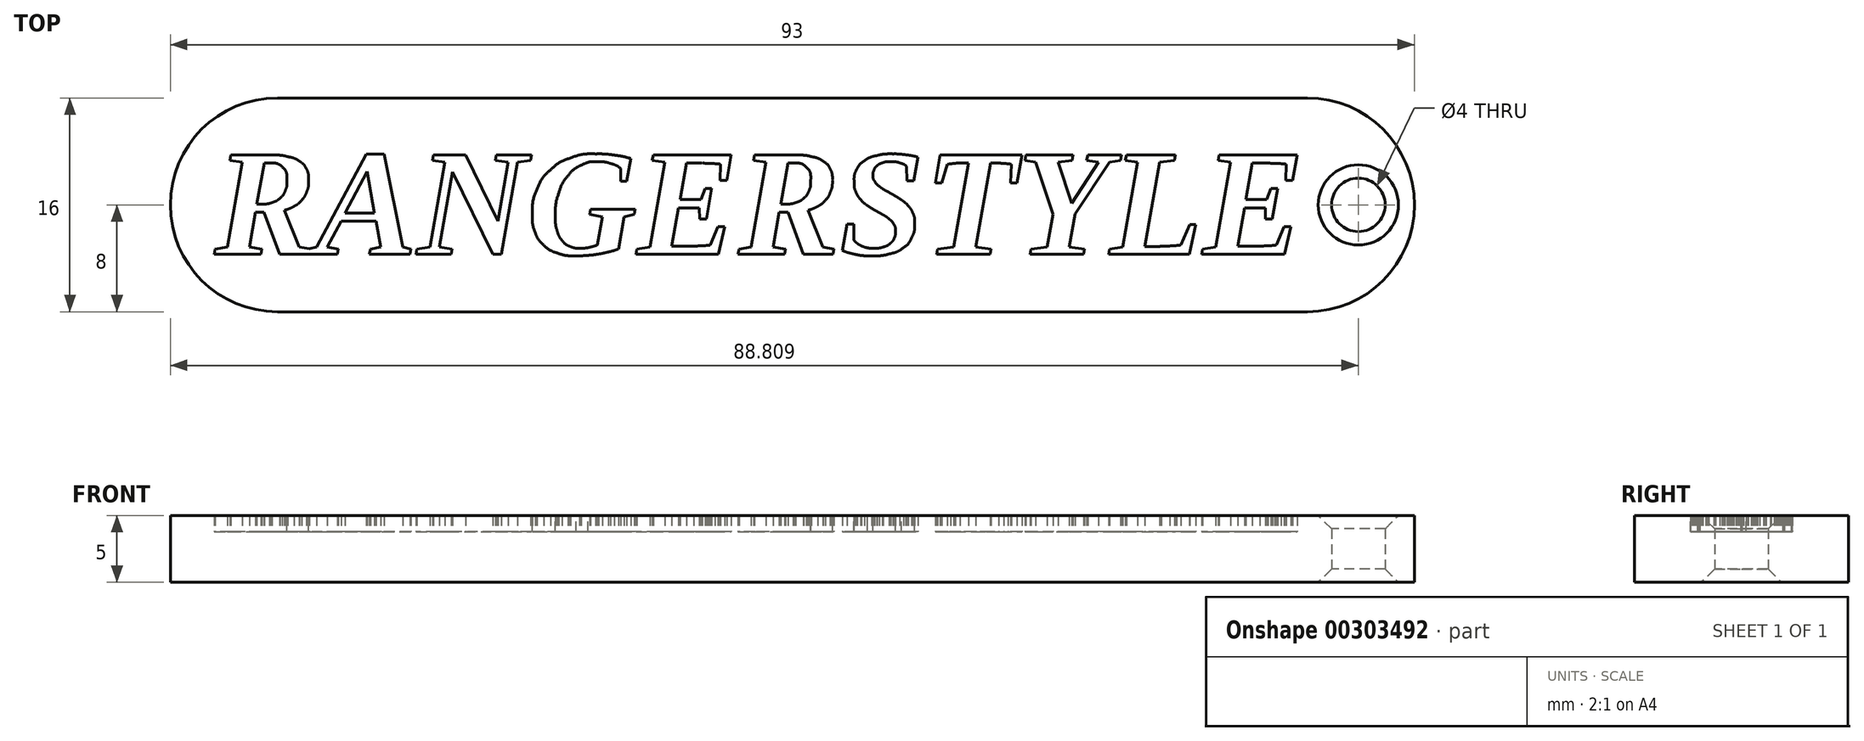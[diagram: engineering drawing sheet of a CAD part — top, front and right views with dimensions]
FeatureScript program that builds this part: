
annotation { "Feature Type Name" : "Feature", "Feature Type Description" : "" }
export const myFeature = defineFeature(function(context is Context, id is Id, definition is map)
    precondition{}
    {
        {
            var Q0;
            Q0=qCreatedBy(makeId("Top.planeOp"),FACE);
            var sketch = newSketch(context, id + "F0", { "sketchPlane" : qUnion([Q0])});
            skFitSpline(sketch, "E0", {"points": [v(-36.27, 3.73) * mm, v(-35.77, 3.73) * mm, v(-35.34, 3.69) * mm, v(-34.99, 3.6) * mm]});
            skFitSpline(sketch, "E1", {"points": [v(-34.99, 3.6) * mm, v(-34.63, 3.53) * mm, v(-34.33, 3.41) * mm, v(-34.1, 3.25) * mm]});
            skFitSpline(sketch, "E2", {"points": [v(-34.1, 3.25) * mm, v(-33.87, 3.1) * mm, v(-33.7, 2.9) * mm, v(-33.59, 2.67) * mm]});
            skFitSpline(sketch, "E3", {"points": [v(-33.59, 2.67) * mm, v(-33.48, 2.44) * mm, v(-33.42, 2.17) * mm, v(-33.42, 1.86) * mm]});
            skFitSpline(sketch, "E4", {"points": [v(-33.42, 1.86) * mm, v(-33.42, 1.54) * mm, v(-33.47, 1.25) * mm, v(-33.56, 1) * mm]});
            skFitSpline(sketch, "E5", {"points": [v(-33.56, 1) * mm, v(-33.65, 0.75) * mm, v(-33.78, 0.53) * mm, v(-33.94, 0.35) * mm]});
            skFitSpline(sketch, "E6", {"points": [v(-33.94, 0.35) * mm, v(-34.1, 0.17) * mm, v(-34.3, 0.01) * mm, v(-34.53, -0.11) * mm]});
            skFitSpline(sketch, "E7", {"points": [v(-34.53, -0.11) * mm, v(-34.75, -0.23) * mm, v(-34.99, -0.33) * mm, v(-35.25, -0.4) * mm]});
            skLineSegment(sketch, "E8", {"start": v(-37.4, -0.55) * mm, "end": v(-37.86, -3.15) * mm});
            skLineSegment(sketch, "E9", {"start": v(-37.86, -3.15) * mm, "end": v(-36.93, -3.3) * mm});
            skLineSegment(sketch, "E10", {"start": v(-36.93, -3.3) * mm, "end": v(-37, -3.7) * mm});
            skLineSegment(sketch, "E11", {"start": v(-37, -3.7) * mm, "end": v(-40.47, -3.7) * mm});
            skLineSegment(sketch, "E12", {"start": v(-40.47, -3.7) * mm, "end": v(-40.4, -3.3) * mm});
            skLineSegment(sketch, "E13", {"start": v(-40.4, -3.3) * mm, "end": v(-39.5, -3.15) * mm});
            skLineSegment(sketch, "E14", {"start": v(-39.5, -3.15) * mm, "end": v(-38.38, 3.18) * mm});
            skLineSegment(sketch, "E15", {"start": v(-38.38, 3.18) * mm, "end": v(-39.3, 3.33) * mm});
            skLineSegment(sketch, "E16", {"start": v(-39.3, 3.33) * mm, "end": v(-39.24, 3.73) * mm});
            skLineSegment(sketch, "E17", {"start": v(-39.24, 3.73) * mm, "end": v(-36.27, 3.73) * mm});
            skFitSpline(sketch, "E18", {"points": [v(-36.99, 0.06) * mm, v(-36.68, 0.06) * mm, v(-36.41, 0.1) * mm, v(-36.17, 0.17) * mm]});
            skFitSpline(sketch, "E19", {"points": [v(-36.17, 0.17) * mm, v(-35.93, 0.25) * mm, v(-35.73, 0.36) * mm, v(-35.56, 0.5) * mm]});
            skFitSpline(sketch, "E20", {"points": [v(-35.56, 0.5) * mm, v(-35.4, 0.65) * mm, v(-35.27, 0.83) * mm, v(-35.18, 1.04) * mm]});
            skFitSpline(sketch, "E21", {"points": [v(-35.18, 1.04) * mm, v(-35.1, 1.26) * mm, v(-35.05, 1.5) * mm, v(-35.05, 1.77) * mm]});
            skFitSpline(sketch, "E22", {"points": [v(-35.05, 1.77) * mm, v(-35.05, 2.25) * mm, v(-35.16, 2.6) * mm, v(-35.39, 2.8) * mm]});
            skFitSpline(sketch, "E23", {"points": [v(-35.39, 2.8) * mm, v(-35.6, 3.02) * mm, v(-35.93, 3.12) * mm, v(-36.37, 3.12) * mm]});
            skLineSegment(sketch, "E24", {"start": v(-35.25, -0.4) * mm, "end": v(-34.13, -3.15) * mm});
            skLineSegment(sketch, "E25", {"start": v(-34.13, -3.15) * mm, "end": v(-33.32, -3.3) * mm});
            skLineSegment(sketch, "E26", {"start": v(-33.32, -3.3) * mm, "end": v(-33.38, -3.7) * mm});
            skLineSegment(sketch, "E27", {"start": v(-33.38, -3.7) * mm, "end": v(-35.6, -3.7) * mm});
            skLineSegment(sketch, "E28", {"start": v(-35.6, -3.7) * mm, "end": v(-36.75, -0.55) * mm});
            skLineSegment(sketch, "E29", {"start": v(-36.75, -0.55) * mm, "end": v(-37.4, -0.55) * mm});
            skLineSegment(sketch, "E30", {"start": v(-36.37, 3.12) * mm, "end": v(-36.75, 3.12) * mm});
            skLineSegment(sketch, "E31", {"start": v(-36.75, 3.12) * mm, "end": v(-37.3, 0.06) * mm});
            skLineSegment(sketch, "E32", {"start": v(-37.3, 0.06) * mm, "end": v(-36.99, 0.06) * mm});
            skLineSegment(sketch, "E33", {"start": v(-31.2, -3.3) * mm, "end": v(-31.28, -3.7) * mm});
            skLineSegment(sketch, "E34", {"start": v(-31.28, -3.7) * mm, "end": v(-33.46, -3.7) * mm});
            skLineSegment(sketch, "E35", {"start": v(-33.46, -3.7) * mm, "end": v(-33.38, -3.3) * mm});
            skLineSegment(sketch, "E36", {"start": v(-33.38, -3.3) * mm, "end": v(-32.81, -3.15) * mm});
            skLineSegment(sketch, "E37", {"start": v(-32.81, -3.15) * mm, "end": v(-29.11, 3.8) * mm});
            skLineSegment(sketch, "E38", {"start": v(-29.11, 3.8) * mm, "end": v(-27.78, 3.8) * mm});
            skLineSegment(sketch, "E39", {"start": v(-27.78, 3.8) * mm, "end": v(-26.37, -3.15) * mm});
            skLineSegment(sketch, "E40", {"start": v(-26.37, -3.15) * mm, "end": v(-25.77, -3.3) * mm});
            skLineSegment(sketch, "E41", {"start": v(-25.77, -3.3) * mm, "end": v(-25.85, -3.7) * mm});
            skLineSegment(sketch, "E42", {"start": v(-25.85, -3.7) * mm, "end": v(-28.89, -3.7) * mm});
            skLineSegment(sketch, "E43", {"start": v(-28.89, -3.7) * mm, "end": v(-28.81, -3.3) * mm});
            skLineSegment(sketch, "E44", {"start": v(-28.81, -3.3) * mm, "end": v(-28.05, -3.15) * mm});
            skLineSegment(sketch, "E45", {"start": v(-28.05, -3.15) * mm, "end": v(-28.38, -1.22) * mm});
            skLineSegment(sketch, "E46", {"start": v(-28.38, -1.22) * mm, "end": v(-31, -1.22) * mm});
            skLineSegment(sketch, "E47", {"start": v(-31, -1.22) * mm, "end": v(-32.02, -3.15) * mm});
            skLineSegment(sketch, "E48", {"start": v(-32.02, -3.15) * mm, "end": v(-31.2, -3.3) * mm});
            skLineSegment(sketch, "E49", {"start": v(-29.06, 2.5) * mm, "end": v(-30.7, -0.62) * mm});
            skLineSegment(sketch, "E50", {"start": v(-30.7, -0.62) * mm, "end": v(-28.5, -0.62) * mm});
            skLineSegment(sketch, "E51", {"start": v(-28.5, -0.62) * mm, "end": v(-29.06, 2.5) * mm});
            skFitSpline(sketch, "E52", {"points": [v(-16.7, -0.8) * mm, v(-16.7, -0.06) * mm, v(-16.58, 0.6) * mm, v(-16.34, 1.17) * mm]});
            skFitSpline(sketch, "E53", {"points": [v(-16.34, 1.17) * mm, v(-16.1, 1.74) * mm, v(-15.76, 2.22) * mm, v(-15.34, 2.62) * mm]});
            skFitSpline(sketch, "E54", {"points": [v(-15.34, 2.62) * mm, v(-14.91, 3) * mm, v(-14.41, 3.3) * mm, v(-13.83, 3.5) * mm]});
            skFitSpline(sketch, "E55", {"points": [v(-13.83, 3.5) * mm, v(-13.26, 3.71) * mm, v(-12.64, 3.81) * mm, v(-11.97, 3.81) * mm]});
            skFitSpline(sketch, "E56", {"points": [v(-11.97, 3.81) * mm, v(-11.46, 3.81) * mm, v(-10.99, 3.78) * mm, v(-10.56, 3.72) * mm]});
            skFitSpline(sketch, "E57", {"points": [v(-10.56, 3.72) * mm, v(-10.14, 3.66) * mm, v(-9.73, 3.58) * mm, v(-9.33, 3.47) * mm]});
            skLineSegment(sketch, "E58", {"start": v(-18.5, 3.18) * mm, "end": v(-19.47, 3.33) * mm});
            skLineSegment(sketch, "E59", {"start": v(-19.47, 3.33) * mm, "end": v(-19.4, 3.73) * mm});
            skLineSegment(sketch, "E60", {"start": v(-19.4, 3.73) * mm, "end": v(-16.76, 3.73) * mm});
            skLineSegment(sketch, "E61", {"start": v(-16.76, 3.73) * mm, "end": v(-16.83, 3.33) * mm});
            skLineSegment(sketch, "E62", {"start": v(-16.83, 3.33) * mm, "end": v(-17.8, 3.18) * mm});
            skLineSegment(sketch, "E63", {"start": v(-17.8, 3.18) * mm, "end": v(-19.02, -3.7) * mm});
            skLineSegment(sketch, "E64", {"start": v(-19.02, -3.7) * mm, "end": v(-19.65, -3.7) * mm});
            skLineSegment(sketch, "E65", {"start": v(-19.65, -3.7) * mm, "end": v(-22.65, 2.46) * mm});
            skLineSegment(sketch, "E66", {"start": v(-22.65, 2.46) * mm, "end": v(-23.66, -3.15) * mm});
            skLineSegment(sketch, "E67", {"start": v(-23.66, -3.15) * mm, "end": v(-22.69, -3.3) * mm});
            skLineSegment(sketch, "E68", {"start": v(-22.69, -3.3) * mm, "end": v(-22.75, -3.7) * mm});
            skLineSegment(sketch, "E69", {"start": v(-22.75, -3.7) * mm, "end": v(-25.4, -3.7) * mm});
            skLineSegment(sketch, "E70", {"start": v(-25.4, -3.7) * mm, "end": v(-25.33, -3.3) * mm});
            skLineSegment(sketch, "E71", {"start": v(-25.33, -3.3) * mm, "end": v(-24.35, -3.15) * mm});
            skLineSegment(sketch, "E72", {"start": v(-24.35, -3.15) * mm, "end": v(-23.24, 3.18) * mm});
            skLineSegment(sketch, "E73", {"start": v(-23.24, 3.18) * mm, "end": v(-24.16, 3.33) * mm});
            skLineSegment(sketch, "E74", {"start": v(-24.16, 3.33) * mm, "end": v(-24.09, 3.73) * mm});
            skLineSegment(sketch, "E75", {"start": v(-24.09, 3.73) * mm, "end": v(-21.69, 3.73) * mm});
            skLineSegment(sketch, "E76", {"start": v(-21.69, 3.73) * mm, "end": v(-19.28, -1.22) * mm});
            skLineSegment(sketch, "E77", {"start": v(-19.28, -1.22) * mm, "end": v(-18.5, 3.18) * mm});
            skFitSpline(sketch, "E78", {"points": [v(-10.1, 2.73) * mm, v(-10.31, 2.89) * mm, v(-10.57, 3.01) * mm, v(-10.87, 3.1) * mm]});
            skFitSpline(sketch, "E79", {"points": [v(-10.87, 3.1) * mm, v(-11.17, 3.19) * mm, v(-11.5, 3.23) * mm, v(-11.87, 3.23) * mm]});
            skFitSpline(sketch, "E80", {"points": [v(-11.87, 3.23) * mm, v(-12.29, 3.23) * mm, v(-12.68, 3.14) * mm, v(-13.06, 2.96) * mm]});
            skFitSpline(sketch, "E81", {"points": [v(-13.06, 2.96) * mm, v(-13.43, 2.78) * mm, v(-13.76, 2.51) * mm, v(-14.05, 2.16) * mm]});
            skFitSpline(sketch, "E82", {"points": [v(-14.05, 2.16) * mm, v(-14.33, 1.81) * mm, v(-14.56, 1.38) * mm, v(-14.73, 0.86) * mm]});
            skFitSpline(sketch, "E83", {"points": [v(-14.73, 0.86) * mm, v(-14.9, 0.35) * mm, v(-14.98, -0.25) * mm, v(-14.98, -0.91) * mm]});
            skFitSpline(sketch, "E84", {"points": [v(-14.98, -0.91) * mm, v(-14.98, -1.3) * mm, v(-14.93, -1.64) * mm, v(-14.84, -1.93) * mm]});
            skFitSpline(sketch, "E85", {"points": [v(-14.84, -1.93) * mm, v(-14.76, -2.23) * mm, v(-14.63, -2.47) * mm, v(-14.47, -2.67) * mm]});
            skFitSpline(sketch, "E86", {"points": [v(-14.47, -2.67) * mm, v(-14.31, -2.86) * mm, v(-14.12, -3) * mm, v(-13.9, -3.1) * mm]});
            skFitSpline(sketch, "E87", {"points": [v(-13.9, -3.1) * mm, v(-13.68, -3.2) * mm, v(-13.43, -3.24) * mm, v(-13.16, -3.24) * mm]});
            skFitSpline(sketch, "E88", {"points": [v(-13.16, -3.24) * mm, v(-12.88, -3.24) * mm, v(-12.62, -3.22) * mm, v(-12.4, -3.16) * mm]});
            skFitSpline(sketch, "E89", {"points": [v(-12.4, -3.16) * mm, v(-12.16, -3.1) * mm, v(-11.98, -3.06) * mm, v(-11.85, -3) * mm]});
            skLineSegment(sketch, "E90", {"start": v(-9.33, 3.47) * mm, "end": v(-9.64, 1.76) * mm});
            skLineSegment(sketch, "E91", {"start": v(-9.64, 1.76) * mm, "end": v(-10.1, 1.76) * mm});
            skLineSegment(sketch, "E92", {"start": v(-10.1, 1.76) * mm, "end": v(-10.1, 2.73) * mm});
            skFitSpline(sketch, "E93", {"points": [v(-10.27, -3.31) * mm, v(-10.51, -3.4) * mm, v(-10.76, -3.46) * mm, v(-11, -3.53) * mm]});
            skFitSpline(sketch, "E94", {"points": [v(-11, -3.53) * mm, v(-11.25, -3.58) * mm, v(-11.5, -3.64) * mm, v(-11.76, -3.68) * mm]});
            skFitSpline(sketch, "E95", {"points": [v(-11.76, -3.68) * mm, v(-12.01, -3.72) * mm, v(-12.28, -3.76) * mm, v(-12.55, -3.78) * mm]});
            skFitSpline(sketch, "E96", {"points": [v(-12.55, -3.78) * mm, v(-12.83, -3.8) * mm, v(-13.12, -3.81) * mm, v(-13.42, -3.81) * mm]});
            skFitSpline(sketch, "E97", {"points": [v(-13.42, -3.81) * mm, v(-13.94, -3.81) * mm, v(-14.41, -3.75) * mm, v(-14.82, -3.6) * mm]});
            skFitSpline(sketch, "E98", {"points": [v(-14.82, -3.6) * mm, v(-15.23, -3.47) * mm, v(-15.57, -3.27) * mm, v(-15.85, -3) * mm]});
            skFitSpline(sketch, "E99", {"points": [v(-15.85, -3) * mm, v(-16.13, -2.75) * mm, v(-16.34, -2.43) * mm, v(-16.48, -2.06) * mm]});
            skFitSpline(sketch, "E100", {"points": [v(-16.48, -2.06) * mm, v(-16.63, -1.69) * mm, v(-16.7, -1.27) * mm, v(-16.7, -0.8) * mm]});
            skLineSegment(sketch, "E101", {"start": v(-11.85, -3) * mm, "end": v(-11.47, -0.9) * mm});
            skLineSegment(sketch, "E102", {"start": v(-11.47, -0.9) * mm, "end": v(-12.4, -0.72) * mm});
            skLineSegment(sketch, "E103", {"start": v(-12.4, -0.72) * mm, "end": v(-12.33, -0.34) * mm});
            skLineSegment(sketch, "E104", {"start": v(-12.33, -0.34) * mm, "end": v(-9.02, -0.34) * mm});
            skLineSegment(sketch, "E105", {"start": v(-9.02, -0.34) * mm, "end": v(-9.08, -0.72) * mm});
            skLineSegment(sketch, "E106", {"start": v(-9.08, -0.72) * mm, "end": v(-9.84, -0.9) * mm});
            skLineSegment(sketch, "E107", {"start": v(-9.84, -0.9) * mm, "end": v(-10.27, -3.31) * mm});
            skFitSpline(sketch, "E108", {"points": [v(-2.63, 3.04) * mm, v(-2.75, 3.06) * mm, v(-2.88, 3.07) * mm, v(-3.04, 3.08) * mm]});
            skFitSpline(sketch, "E109", {"points": [v(-3.04, 3.08) * mm, v(-3.19, 3.1) * mm, v(-3.35, 3.1) * mm, v(-3.51, 3.1) * mm]});
            skFitSpline(sketch, "E110", {"points": [v(-3.51, 3.1) * mm, v(-3.68, 3.11) * mm, v(-3.84, 3.12) * mm, v(-4, 3.12) * mm]});
            skFitSpline(sketch, "E111", {"points": [v(-4, 3.12) * mm, v(-4.15, 3.12) * mm, v(-4.3, 3.12) * mm, v(-4.41, 3.12) * mm]});
            skLineSegment(sketch, "E112", {"start": v(-8.9, -3.3) * mm, "end": v(-7.92, -3.15) * mm});
            skLineSegment(sketch, "E113", {"start": v(-7.92, -3.15) * mm, "end": v(-6.8, 3.18) * mm});
            skLineSegment(sketch, "E114", {"start": v(-6.8, 3.18) * mm, "end": v(-7.73, 3.33) * mm});
            skLineSegment(sketch, "E115", {"start": v(-7.73, 3.33) * mm, "end": v(-7.66, 3.73) * mm});
            skLineSegment(sketch, "E116", {"start": v(-7.66, 3.73) * mm, "end": v(-1.83, 3.73) * mm});
            skLineSegment(sketch, "E117", {"start": v(-1.83, 3.73) * mm, "end": v(-2.16, 1.84) * mm});
            skLineSegment(sketch, "E118", {"start": v(-2.16, 1.84) * mm, "end": v(-2.67, 1.84) * mm});
            skLineSegment(sketch, "E119", {"start": v(-2.67, 1.84) * mm, "end": v(-2.63, 3.04) * mm});
            skFitSpline(sketch, "E120", {"points": [v(-5.26, -3.1) * mm, v(-5.03, -3.1) * mm, v(-4.82, -3.1) * mm, v(-4.62, -3.09) * mm]});
            skFitSpline(sketch, "E121", {"points": [v(-4.62, -3.09) * mm, v(-4.41, -3.08) * mm, v(-4.23, -3.07) * mm, v(-4.07, -3.07) * mm]});
            skFitSpline(sketch, "E122", {"points": [v(-4.07, -3.07) * mm, v(-3.9, -3.06) * mm, v(-3.77, -3.05) * mm, v(-3.65, -3.04) * mm]});
            skFitSpline(sketch, "E123", {"points": [v(-3.65, -3.04) * mm, v(-3.53, -3.03) * mm, v(-3.45, -3.02) * mm, v(-3.39, -3) * mm]});
            skLineSegment(sketch, "E124", {"start": v(-4.41, 3.12) * mm, "end": v(-5.18, 3.12) * mm});
            skLineSegment(sketch, "E125", {"start": v(-5.18, 3.12) * mm, "end": v(-5.66, 0.4) * mm});
            skLineSegment(sketch, "E126", {"start": v(-5.66, 0.4) * mm, "end": v(-4.1, 0.4) * mm});
            skLineSegment(sketch, "E127", {"start": v(-4.1, 0.4) * mm, "end": v(-3.79, 1.21) * mm});
            skLineSegment(sketch, "E128", {"start": v(-3.79, 1.21) * mm, "end": v(-3.3, 1.21) * mm});
            skLineSegment(sketch, "E129", {"start": v(-3.3, 1.21) * mm, "end": v(-3.7, -1.07) * mm});
            skLineSegment(sketch, "E130", {"start": v(-3.7, -1.07) * mm, "end": v(-4.2, -1.07) * mm});
            skLineSegment(sketch, "E131", {"start": v(-4.2, -1.07) * mm, "end": v(-4.21, -0.23) * mm});
            skLineSegment(sketch, "E132", {"start": v(-4.21, -0.23) * mm, "end": v(-5.77, -0.23) * mm});
            skLineSegment(sketch, "E133", {"start": v(-5.77, -0.23) * mm, "end": v(-6.27, -3.1) * mm});
            skLineSegment(sketch, "E134", {"start": v(-6.27, -3.1) * mm, "end": v(-5.26, -3.1) * mm});
            skLineSegment(sketch, "E135", {"start": v(-3.39, -3) * mm, "end": v(-2.82, -1.63) * mm});
            skLineSegment(sketch, "E136", {"start": v(-2.82, -1.63) * mm, "end": v(-2.31, -1.63) * mm});
            skLineSegment(sketch, "E137", {"start": v(-2.31, -1.63) * mm, "end": v(-2.78, -3.7) * mm});
            skLineSegment(sketch, "E138", {"start": v(-2.78, -3.7) * mm, "end": v(-8.97, -3.7) * mm});
            skLineSegment(sketch, "E139", {"start": v(-8.97, -3.7) * mm, "end": v(-8.9, -3.3) * mm});
            skLineSegment(sketch, "E140", {"start": v(-8.9, -3.3) * mm, "end": v(-8.9, -3.3) * mm});
            skLineSegment(sketch, "E141", {"start": v(-5.04, -3.1) * mm, "end": v(-3.39, -3) * mm});
            skFitSpline(sketch, "E142", {"points": [v(2.88, 3.73) * mm, v(3.38, 3.73) * mm, v(3.8, 3.69) * mm, v(4.17, 3.6) * mm]});
            skFitSpline(sketch, "E143", {"points": [v(4.17, 3.6) * mm, v(4.53, 3.53) * mm, v(4.82, 3.41) * mm, v(5.05, 3.25) * mm]});
            skFitSpline(sketch, "E144", {"points": [v(5.05, 3.25) * mm, v(5.28, 3.1) * mm, v(5.45, 2.9) * mm, v(5.57, 2.67) * mm]});
            skFitSpline(sketch, "E145", {"points": [v(5.57, 2.67) * mm, v(5.68, 2.44) * mm, v(5.73, 2.17) * mm, v(5.73, 1.86) * mm]});
            skFitSpline(sketch, "E146", {"points": [v(5.73, 1.86) * mm, v(5.73, 1.54) * mm, v(5.69, 1.25) * mm, v(5.6, 1) * mm]});
            skFitSpline(sketch, "E147", {"points": [v(5.6, 1) * mm, v(5.5, 0.75) * mm, v(5.37, 0.53) * mm, v(5.21, 0.35) * mm]});
            skFitSpline(sketch, "E148", {"points": [v(5.21, 0.35) * mm, v(5.05, 0.17) * mm, v(4.85, 0.01) * mm, v(4.63, -0.11) * mm]});
            skFitSpline(sketch, "E149", {"points": [v(4.63, -0.11) * mm, v(4.4, -0.23) * mm, v(4.17, -0.33) * mm, v(3.9, -0.4) * mm]});
            skLineSegment(sketch, "E150", {"start": v(1.76, -0.55) * mm, "end": v(1.3, -3.15) * mm});
            skLineSegment(sketch, "E151", {"start": v(1.3, -3.15) * mm, "end": v(2.22, -3.3) * mm});
            skLineSegment(sketch, "E152", {"start": v(2.22, -3.3) * mm, "end": v(2.16, -3.7) * mm});
            skLineSegment(sketch, "E153", {"start": v(2.16, -3.7) * mm, "end": v(-1.32, -3.7) * mm});
            skLineSegment(sketch, "E154", {"start": v(-1.32, -3.7) * mm, "end": v(-1.25, -3.3) * mm});
            skLineSegment(sketch, "E155", {"start": v(-1.25, -3.3) * mm, "end": v(-0.34, -3.15) * mm});
            skLineSegment(sketch, "E156", {"start": v(-0.34, -3.15) * mm, "end": v(0.77, 3.18) * mm});
            skLineSegment(sketch, "E157", {"start": v(0.77, 3.18) * mm, "end": v(-0.16, 3.33) * mm});
            skLineSegment(sketch, "E158", {"start": v(-0.16, 3.33) * mm, "end": v(-0.08, 3.73) * mm});
            skLineSegment(sketch, "E159", {"start": v(-0.08, 3.73) * mm, "end": v(2.88, 3.73) * mm});
            skFitSpline(sketch, "E160", {"points": [v(2.17, 0.06) * mm, v(2.47, 0.06) * mm, v(2.74, 0.1) * mm, v(2.98, 0.17) * mm]});
            skFitSpline(sketch, "E161", {"points": [v(2.98, 0.17) * mm, v(3.22, 0.25) * mm, v(3.43, 0.36) * mm, v(3.6, 0.5) * mm]});
            skFitSpline(sketch, "E162", {"points": [v(3.6, 0.5) * mm, v(3.76, 0.65) * mm, v(3.89, 0.83) * mm, v(3.97, 1.04) * mm]});
            skFitSpline(sketch, "E163", {"points": [v(3.97, 1.04) * mm, v(4.06, 1.26) * mm, v(4.1, 1.5) * mm, v(4.1, 1.77) * mm]});
            skFitSpline(sketch, "E164", {"points": [v(4.1, 1.77) * mm, v(4.1, 2.25) * mm, v(4, 2.6) * mm, v(3.77, 2.8) * mm]});
            skFitSpline(sketch, "E165", {"points": [v(3.77, 2.8) * mm, v(3.55, 3.02) * mm, v(3.22, 3.12) * mm, v(2.79, 3.12) * mm]});
            skLineSegment(sketch, "E166", {"start": v(3.9, -0.4) * mm, "end": v(5.02, -3.15) * mm});
            skLineSegment(sketch, "E167", {"start": v(5.02, -3.15) * mm, "end": v(5.84, -3.3) * mm});
            skLineSegment(sketch, "E168", {"start": v(5.84, -3.3) * mm, "end": v(5.77, -3.7) * mm});
            skLineSegment(sketch, "E169", {"start": v(5.77, -3.7) * mm, "end": v(3.55, -3.7) * mm});
            skLineSegment(sketch, "E170", {"start": v(3.55, -3.7) * mm, "end": v(2.4, -0.55) * mm});
            skLineSegment(sketch, "E171", {"start": v(2.4, -0.55) * mm, "end": v(1.76, -0.55) * mm});
            skFitSpline(sketch, "E172", {"points": [v(8.67, -3.81) * mm, v(8.2, -3.81) * mm, v(7.76, -3.77) * mm, v(7.4, -3.7) * mm]});
            skFitSpline(sketch, "E173", {"points": [v(7.4, -3.7) * mm, v(7.03, -3.6) * mm, v(6.73, -3.52) * mm, v(6.49, -3.42) * mm]});
            skLineSegment(sketch, "E174", {"start": v(2.79, 3.12) * mm, "end": v(2.4, 3.12) * mm});
            skLineSegment(sketch, "E175", {"start": v(2.4, 3.12) * mm, "end": v(1.86, 0.06) * mm});
            skLineSegment(sketch, "E176", {"start": v(1.86, 0.06) * mm, "end": v(2.17, 0.06) * mm});
            skFitSpline(sketch, "E177", {"points": [v(7.33, -2.62) * mm, v(7.4, -2.7) * mm, v(7.48, -2.8) * mm, v(7.58, -2.87) * mm]});
            skFitSpline(sketch, "E178", {"points": [v(7.58, -2.87) * mm, v(7.68, -2.95) * mm, v(7.8, -3.02) * mm, v(7.92, -3.08) * mm]});
            skFitSpline(sketch, "E179", {"points": [v(7.92, -3.08) * mm, v(8.05, -3.13) * mm, v(8.18, -3.18) * mm, v(8.33, -3.2) * mm]});
            skFitSpline(sketch, "E180", {"points": [v(8.33, -3.2) * mm, v(8.47, -3.24) * mm, v(8.62, -3.25) * mm, v(8.77, -3.25) * mm]});
            skFitSpline(sketch, "E181", {"points": [v(8.77, -3.25) * mm, v(9.06, -3.25) * mm, v(9.31, -3.22) * mm, v(9.52, -3.16) * mm]});
            skFitSpline(sketch, "E182", {"points": [v(9.52, -3.16) * mm, v(9.74, -3.1) * mm, v(9.91, -3) * mm, v(10.05, -2.89) * mm]});
            skFitSpline(sketch, "E183", {"points": [v(10.05, -2.89) * mm, v(10.19, -2.77) * mm, v(10.29, -2.64) * mm, v(10.35, -2.48) * mm]});
            skFitSpline(sketch, "E184", {"points": [v(10.35, -2.48) * mm, v(10.42, -2.33) * mm, v(10.45, -2.16) * mm, v(10.45, -1.98) * mm]});
            skFitSpline(sketch, "E185", {"points": [v(10.45, -1.98) * mm, v(10.45, -1.78) * mm, v(10.4, -1.6) * mm, v(10.32, -1.46) * mm]});
            skFitSpline(sketch, "E186", {"points": [v(10.32, -1.46) * mm, v(10.23, -1.3) * mm, v(10.11, -1.18) * mm, v(9.97, -1.06) * mm]});
            skFitSpline(sketch, "E187", {"points": [v(9.97, -1.06) * mm, v(9.82, -0.94) * mm, v(9.66, -0.82) * mm, v(9.47, -0.72) * mm]});
            skFitSpline(sketch, "E188", {"points": [v(9.47, -0.72) * mm, v(9.29, -0.61) * mm, v(9.1, -0.5) * mm, v(8.9, -0.4) * mm]});
            skFitSpline(sketch, "E189", {"points": [v(8.9, -0.4) * mm, v(8.7, -0.29) * mm, v(8.52, -0.17) * mm, v(8.34, -0.04) * mm]});
            skFitSpline(sketch, "E190", {"points": [v(8.34, -0.04) * mm, v(8.15, 0.08) * mm, v(7.99, 0.23) * mm, v(7.84, 0.4) * mm]});
            skFitSpline(sketch, "E191", {"points": [v(7.84, 0.4) * mm, v(7.7, 0.57) * mm, v(7.58, 0.76) * mm, v(7.49, 0.97) * mm]});
            skFitSpline(sketch, "E192", {"points": [v(7.49, 0.97) * mm, v(7.4, 1.18) * mm, v(7.36, 1.44) * mm, v(7.36, 1.72) * mm]});
            skFitSpline(sketch, "E193", {"points": [v(7.36, 1.72) * mm, v(7.36, 2.08) * mm, v(7.42, 2.39) * mm, v(7.55, 2.64) * mm]});
            skFitSpline(sketch, "E194", {"points": [v(7.55, 2.64) * mm, v(7.68, 2.9) * mm, v(7.87, 3.12) * mm, v(8.12, 3.3) * mm]});
            skFitSpline(sketch, "E195", {"points": [v(8.12, 3.3) * mm, v(8.37, 3.47) * mm, v(8.68, 3.6) * mm, v(9.03, 3.69) * mm]});
            skFitSpline(sketch, "E196", {"points": [v(9.03, 3.69) * mm, v(9.4, 3.77) * mm, v(9.8, 3.81) * mm, v(10.25, 3.81) * mm]});
            skFitSpline(sketch, "E197", {"points": [v(10.25, 3.81) * mm, v(10.57, 3.81) * mm, v(10.89, 3.8) * mm, v(11.22, 3.75) * mm]});
            skFitSpline(sketch, "E198", {"points": [v(11.22, 3.75) * mm, v(11.55, 3.7) * mm, v(11.85, 3.65) * mm, v(12.12, 3.58) * mm]});
            skLineSegment(sketch, "E199", {"start": v(6.49, -3.42) * mm, "end": v(6.84, -1.42) * mm});
            skLineSegment(sketch, "E200", {"start": v(6.84, -1.42) * mm, "end": v(7.33, -1.42) * mm});
            skLineSegment(sketch, "E201", {"start": v(7.33, -1.42) * mm, "end": v(7.33, -2.62) * mm});
            skFitSpline(sketch, "E202", {"points": [v(11.27, 2.9) * mm, v(11.13, 3) * mm, v(10.96, 3.08) * mm, v(10.76, 3.14) * mm]});
            skFitSpline(sketch, "E203", {"points": [v(10.76, 3.14) * mm, v(10.57, 3.2) * mm, v(10.35, 3.24) * mm, v(10.1, 3.24) * mm]});
            skFitSpline(sketch, "E204", {"points": [v(10.1, 3.24) * mm, v(9.87, 3.24) * mm, v(9.66, 3.2) * mm, v(9.5, 3.15) * mm]});
            skFitSpline(sketch, "E205", {"points": [v(9.5, 3.15) * mm, v(9.32, 3.1) * mm, v(9.19, 3.02) * mm, v(9.08, 2.93) * mm]});
            skFitSpline(sketch, "E206", {"points": [v(9.08, 2.93) * mm, v(8.97, 2.84) * mm, v(8.9, 2.73) * mm, v(8.84, 2.6) * mm]});
            skFitSpline(sketch, "E207", {"points": [v(8.84, 2.6) * mm, v(8.79, 2.48) * mm, v(8.76, 2.36) * mm, v(8.76, 2.22) * mm]});
            skFitSpline(sketch, "E208", {"points": [v(8.76, 2.22) * mm, v(8.76, 2.05) * mm, v(8.8, 1.89) * mm, v(8.9, 1.75) * mm]});
            skFitSpline(sketch, "E209", {"points": [v(8.9, 1.75) * mm, v(8.98, 1.61) * mm, v(9.1, 1.49) * mm, v(9.25, 1.37) * mm]});
            skFitSpline(sketch, "E210", {"points": [v(9.25, 1.37) * mm, v(9.4, 1.26) * mm, v(9.57, 1.15) * mm, v(9.75, 1.05) * mm]});
            skFitSpline(sketch, "E211", {"points": [v(9.75, 1.05) * mm, v(9.94, 0.94) * mm, v(10.13, 0.84) * mm, v(10.32, 0.73) * mm]});
            skFitSpline(sketch, "E212", {"points": [v(10.32, 0.73) * mm, v(10.52, 0.62) * mm, v(10.7, 0.5) * mm, v(10.9, 0.37) * mm]});
            skFitSpline(sketch, "E213", {"points": [v(10.9, 0.37) * mm, v(11.08, 0.24) * mm, v(11.25, 0.1) * mm, v(11.4, -0.07) * mm]});
            skFitSpline(sketch, "E214", {"points": [v(11.4, -0.07) * mm, v(11.54, -0.23) * mm, v(11.66, -0.42) * mm, v(11.75, -0.63) * mm]});
            skFitSpline(sketch, "E215", {"points": [v(11.75, -0.63) * mm, v(11.84, -0.84) * mm, v(11.88, -1.08) * mm, v(11.88, -1.36) * mm]});
            skFitSpline(sketch, "E216", {"points": [v(11.88, -1.36) * mm, v(11.88, -1.76) * mm, v(11.81, -2.12) * mm, v(11.67, -2.43) * mm]});
            skFitSpline(sketch, "E217", {"points": [v(11.67, -2.43) * mm, v(11.53, -2.73) * mm, v(11.32, -3) * mm, v(11.05, -3.2) * mm]});
            skFitSpline(sketch, "E218", {"points": [v(11.05, -3.2) * mm, v(10.77, -3.4) * mm, v(10.44, -3.55) * mm, v(10.04, -3.66) * mm]});
            skFitSpline(sketch, "E219", {"points": [v(10.04, -3.66) * mm, v(9.64, -3.76) * mm, v(9.19, -3.81) * mm, v(8.67, -3.81) * mm]});
            skLineSegment(sketch, "E220", {"start": v(12.12, 3.58) * mm, "end": v(11.8, 1.8) * mm});
            skLineSegment(sketch, "E221", {"start": v(11.8, 1.8) * mm, "end": v(11.31, 1.8) * mm});
            skLineSegment(sketch, "E222", {"start": v(11.31, 1.8) * mm, "end": v(11.27, 2.9) * mm});
            skFitSpline(sketch, "E223", {"points": [v(15.57, 3.14) * mm, v(15.48, 3.14) * mm, v(15.39, 3.14) * mm, v(15.27, 3.13) * mm]});
            skFitSpline(sketch, "E224", {"points": [v(15.27, 3.13) * mm, v(15.16, 3.13) * mm, v(15.04, 3.12) * mm, v(14.92, 3.1) * mm]});
            skFitSpline(sketch, "E225", {"points": [v(14.92, 3.1) * mm, v(14.8, 3.1) * mm, v(14.7, 3.09) * mm, v(14.59, 3.07) * mm]});
            skFitSpline(sketch, "E226", {"points": [v(14.59, 3.07) * mm, v(14.48, 3.06) * mm, v(14.4, 3.05) * mm, v(14.32, 3.03) * mm]});
            skLineSegment(sketch, "E227", {"start": v(13.52, -3.7) * mm, "end": v(13.6, -3.3) * mm});
            skLineSegment(sketch, "E228", {"start": v(13.6, -3.3) * mm, "end": v(14.8, -3.15) * mm});
            skLineSegment(sketch, "E229", {"start": v(14.8, -3.15) * mm, "end": v(15.9, 3.14) * mm});
            skLineSegment(sketch, "E230", {"start": v(15.9, 3.14) * mm, "end": v(15.57, 3.14) * mm});
            skFitSpline(sketch, "E231", {"points": [v(19.12, 3.03) * mm, v(19.06, 3.05) * mm, v(18.97, 3.06) * mm, v(18.86, 3.07) * mm]});
            skFitSpline(sketch, "E232", {"points": [v(18.86, 3.07) * mm, v(18.76, 3.08) * mm, v(18.65, 3.1) * mm, v(18.53, 3.1) * mm]});
            skFitSpline(sketch, "E233", {"points": [v(18.53, 3.1) * mm, v(18.41, 3.1) * mm, v(18.3, 3.12) * mm, v(18.18, 3.12) * mm]});
            skFitSpline(sketch, "E234", {"points": [v(18.18, 3.12) * mm, v(18.06, 3.13) * mm, v(17.96, 3.13) * mm, v(17.88, 3.13) * mm]});
            skLineSegment(sketch, "E235", {"start": v(14.32, 3.03) * mm, "end": v(13.9, 1.65) * mm});
            skLineSegment(sketch, "E236", {"start": v(13.9, 1.65) * mm, "end": v(13.42, 1.65) * mm});
            skLineSegment(sketch, "E237", {"start": v(13.42, 1.65) * mm, "end": v(13.8, 3.73) * mm});
            skLineSegment(sketch, "E238", {"start": v(13.8, 3.73) * mm, "end": v(19.9, 3.73) * mm});
            skLineSegment(sketch, "E239", {"start": v(19.9, 3.73) * mm, "end": v(19.54, 1.65) * mm});
            skLineSegment(sketch, "E240", {"start": v(19.54, 1.65) * mm, "end": v(19.05, 1.65) * mm});
            skLineSegment(sketch, "E241", {"start": v(19.05, 1.65) * mm, "end": v(19.12, 3.03) * mm});
            skLineSegment(sketch, "E242", {"start": v(17.88, 3.13) * mm, "end": v(17.55, 3.13) * mm});
            skLineSegment(sketch, "E243", {"start": v(17.55, 3.13) * mm, "end": v(16.44, -3.15) * mm});
            skLineSegment(sketch, "E244", {"start": v(16.44, -3.15) * mm, "end": v(17.6, -3.3) * mm});
            skLineSegment(sketch, "E245", {"start": v(17.6, -3.3) * mm, "end": v(17.53, -3.7) * mm});
            skLineSegment(sketch, "E246", {"start": v(17.53, -3.7) * mm, "end": v(13.52, -3.7) * mm});
            skLineSegment(sketch, "E247", {"start": v(23.87, -0.67) * mm, "end": v(23.43, -3.15) * mm});
            skLineSegment(sketch, "E248", {"start": v(23.43, -3.15) * mm, "end": v(24.58, -3.3) * mm});
            skLineSegment(sketch, "E249", {"start": v(24.58, -3.3) * mm, "end": v(24.52, -3.7) * mm});
            skLineSegment(sketch, "E250", {"start": v(24.52, -3.7) * mm, "end": v(20.51, -3.7) * mm});
            skLineSegment(sketch, "E251", {"start": v(20.51, -3.7) * mm, "end": v(20.58, -3.3) * mm});
            skLineSegment(sketch, "E252", {"start": v(20.58, -3.3) * mm, "end": v(21.79, -3.15) * mm});
            skLineSegment(sketch, "E253", {"start": v(21.79, -3.15) * mm, "end": v(22.23, -0.7) * mm});
            skLineSegment(sketch, "E254", {"start": v(22.23, -0.7) * mm, "end": v(20.93, 3.18) * mm});
            skLineSegment(sketch, "E255", {"start": v(20.93, 3.18) * mm, "end": v(20.12, 3.33) * mm});
            skLineSegment(sketch, "E256", {"start": v(20.12, 3.33) * mm, "end": v(20.2, 3.73) * mm});
            skLineSegment(sketch, "E257", {"start": v(20.2, 3.73) * mm, "end": v(23.72, 3.73) * mm});
            skLineSegment(sketch, "E258", {"start": v(23.72, 3.73) * mm, "end": v(23.65, 3.33) * mm});
            skLineSegment(sketch, "E259", {"start": v(23.65, 3.33) * mm, "end": v(22.62, 3.18) * mm});
            skLineSegment(sketch, "E260", {"start": v(22.62, 3.18) * mm, "end": v(23.6, 0.1) * mm});
            skLineSegment(sketch, "E261", {"start": v(23.6, 0.1) * mm, "end": v(25.62, 3.18) * mm});
            skLineSegment(sketch, "E262", {"start": v(25.62, 3.18) * mm, "end": v(24.74, 3.33) * mm});
            skLineSegment(sketch, "E263", {"start": v(24.74, 3.33) * mm, "end": v(24.82, 3.73) * mm});
            skLineSegment(sketch, "E264", {"start": v(24.82, 3.73) * mm, "end": v(27.34, 3.73) * mm});
            skLineSegment(sketch, "E265", {"start": v(27.34, 3.73) * mm, "end": v(27.27, 3.33) * mm});
            skLineSegment(sketch, "E266", {"start": v(27.27, 3.33) * mm, "end": v(26.46, 3.18) * mm});
            skLineSegment(sketch, "E267", {"start": v(26.46, 3.18) * mm, "end": v(23.87, -0.67) * mm});
            skFitSpline(sketch, "E268", {"points": [v(29.7, -3.12) * mm, v(29.9, -3.12) * mm, v(30.1, -3.11) * mm, v(30.32, -3.1) * mm]});
            skFitSpline(sketch, "E269", {"points": [v(30.32, -3.1) * mm, v(30.55, -3.1) * mm, v(30.76, -3.09) * mm, v(30.95, -3.08) * mm]});
            skFitSpline(sketch, "E270", {"points": [v(30.95, -3.08) * mm, v(31.15, -3.07) * mm, v(31.32, -3.05) * mm, v(31.47, -3.04) * mm]});
            skFitSpline(sketch, "E271", {"points": [v(31.47, -3.04) * mm, v(31.62, -3.03) * mm, v(31.73, -3.02) * mm, v(31.79, -3) * mm]});
            skLineSegment(sketch, "E272", {"start": v(31.31, 3.33) * mm, "end": v(30.2, 3.18) * mm});
            skLineSegment(sketch, "E273", {"start": v(30.2, 3.18) * mm, "end": v(29.08, -3.12) * mm});
            skLineSegment(sketch, "E274", {"start": v(29.08, -3.12) * mm, "end": v(29.7, -3.12) * mm});
            skLineSegment(sketch, "E275", {"start": v(31.79, -3) * mm, "end": v(32.44, -1.46) * mm});
            skLineSegment(sketch, "E276", {"start": v(32.44, -1.46) * mm, "end": v(32.9, -1.46) * mm});
            skLineSegment(sketch, "E277", {"start": v(32.9, -1.46) * mm, "end": v(32.4, -3.7) * mm});
            skLineSegment(sketch, "E278", {"start": v(32.4, -3.7) * mm, "end": v(26.4, -3.7) * mm});
            skLineSegment(sketch, "E279", {"start": v(26.4, -3.7) * mm, "end": v(26.46, -3.3) * mm});
            skLineSegment(sketch, "E280", {"start": v(26.46, -3.3) * mm, "end": v(27.44, -3.15) * mm});
            skLineSegment(sketch, "E281", {"start": v(27.44, -3.15) * mm, "end": v(28.56, 3.18) * mm});
            skLineSegment(sketch, "E282", {"start": v(28.56, 3.18) * mm, "end": v(27.64, 3.33) * mm});
            skLineSegment(sketch, "E283", {"start": v(27.64, 3.33) * mm, "end": v(27.7, 3.73) * mm});
            skLineSegment(sketch, "E284", {"start": v(27.7, 3.73) * mm, "end": v(31.38, 3.73) * mm});
            skLineSegment(sketch, "E285", {"start": v(31.38, 3.73) * mm, "end": v(31.31, 3.33) * mm});
            skFitSpline(sketch, "E286", {"points": [v(39.67, 3.04) * mm, v(39.56, 3.06) * mm, v(39.42, 3.07) * mm, v(39.27, 3.08) * mm]});
            skFitSpline(sketch, "E287", {"points": [v(39.27, 3.08) * mm, v(39.11, 3.1) * mm, v(38.96, 3.1) * mm, v(38.79, 3.1) * mm]});
            skFitSpline(sketch, "E288", {"points": [v(38.79, 3.1) * mm, v(38.63, 3.11) * mm, v(38.47, 3.12) * mm, v(38.3, 3.12) * mm]});
            skFitSpline(sketch, "E289", {"points": [v(38.3, 3.12) * mm, v(38.15, 3.12) * mm, v(38.01, 3.12) * mm, v(37.9, 3.12) * mm]});
            skLineSegment(sketch, "E290", {"start": v(33.4, -3.3) * mm, "end": v(34.38, -3.15) * mm});
            skLineSegment(sketch, "E291", {"start": v(34.38, -3.15) * mm, "end": v(35.5, 3.18) * mm});
            skLineSegment(sketch, "E292", {"start": v(35.5, 3.18) * mm, "end": v(34.57, 3.33) * mm});
            skLineSegment(sketch, "E293", {"start": v(34.57, 3.33) * mm, "end": v(34.64, 3.73) * mm});
            skLineSegment(sketch, "E294", {"start": v(34.64, 3.73) * mm, "end": v(40.47, 3.73) * mm});
            skLineSegment(sketch, "E295", {"start": v(40.47, 3.73) * mm, "end": v(40.14, 1.84) * mm});
            skLineSegment(sketch, "E296", {"start": v(40.14, 1.84) * mm, "end": v(39.64, 1.84) * mm});
            skLineSegment(sketch, "E297", {"start": v(39.64, 1.84) * mm, "end": v(39.67, 3.04) * mm});
            skFitSpline(sketch, "E298", {"points": [v(37.04, -3.1) * mm, v(37.27, -3.1) * mm, v(37.49, -3.1) * mm, v(37.69, -3.09) * mm]});
            skFitSpline(sketch, "E299", {"points": [v(37.69, -3.09) * mm, v(37.89, -3.08) * mm, v(38.07, -3.07) * mm, v(38.23, -3.07) * mm]});
            skFitSpline(sketch, "E300", {"points": [v(38.23, -3.07) * mm, v(38.4, -3.06) * mm, v(38.54, -3.05) * mm, v(38.65, -3.04) * mm]});
            skFitSpline(sketch, "E301", {"points": [v(38.65, -3.04) * mm, v(38.77, -3.03) * mm, v(38.86, -3.02) * mm, v(38.92, -3) * mm]});
            skLineSegment(sketch, "E302", {"start": v(37.9, 3.12) * mm, "end": v(37.13, 3.12) * mm});
            skLineSegment(sketch, "E303", {"start": v(37.13, 3.12) * mm, "end": v(36.64, 0.4) * mm});
            skLineSegment(sketch, "E304", {"start": v(36.64, 0.4) * mm, "end": v(38.2, 0.4) * mm});
            skLineSegment(sketch, "E305", {"start": v(38.2, 0.4) * mm, "end": v(38.52, 1.21) * mm});
            skLineSegment(sketch, "E306", {"start": v(38.52, 1.21) * mm, "end": v(39.01, 1.21) * mm});
            skLineSegment(sketch, "E307", {"start": v(39.01, 1.21) * mm, "end": v(38.6, -1.07) * mm});
            skLineSegment(sketch, "E308", {"start": v(38.6, -1.07) * mm, "end": v(38.11, -1.07) * mm});
            skLineSegment(sketch, "E309", {"start": v(38.11, -1.07) * mm, "end": v(38.1, -0.23) * mm});
            skLineSegment(sketch, "E310", {"start": v(38.1, -0.23) * mm, "end": v(36.53, -0.23) * mm});
            skLineSegment(sketch, "E311", {"start": v(36.53, -0.23) * mm, "end": v(36.03, -3.1) * mm});
            skLineSegment(sketch, "E312", {"start": v(36.03, -3.1) * mm, "end": v(37.04, -3.1) * mm});
            skLineSegment(sketch, "E313", {"start": v(38.92, -3) * mm, "end": v(39.49, -1.63) * mm});
            skLineSegment(sketch, "E314", {"start": v(39.49, -1.63) * mm, "end": v(40, -1.63) * mm});
            skLineSegment(sketch, "E315", {"start": v(40, -1.63) * mm, "end": v(39.53, -3.7) * mm});
            skLineSegment(sketch, "E316", {"start": v(39.53, -3.7) * mm, "end": v(33.33, -3.7) * mm});
            skLineSegment(sketch, "E317", {"start": v(33.33, -3.7) * mm, "end": v(33.4, -3.3) * mm});
            skLineSegment(sketch, "E318", {"start": v(33.4, -3.3) * mm, "end": v(33.4, -3.3) * mm});
            skLineSegment(sketch, "E319", {"start": v(37.26, -3.1) * mm, "end": v(38.92, -3) * mm});
            skSolve(sketch);
        }
        {
            var Q0;
            Q0=qCreatedBy(makeId("Top.planeOp"),FACE);
            var sketch = newSketch(context, id + "F1", { "sketchPlane" : qUnion([Q0])});
            skLineSegment(sketch, "E320.bottom", {"start": v(-35.76, 8) * mm, "end": v(41.24, 8) * mm});
            skLineSegment(sketch, "E320.top", {"start": v(-35.76, -8) * mm, "end": v(41.24, -8) * mm});
            skLineSegment(sketch, "E320.left", {"start": v(-43.76, 0) * mm, "end": v(-43.76, 0) * mm});
            skLineSegment(sketch, "E320.right", {"start": v(49.24, 0) * mm, "end": v(49.24, 0) * mm});
            skPoint(sketch, "E321.visualSharp", {"position": v(-43.76, -8) * mm});
            skArc(sketch, "E321.filletArc", {"start": v(-43.76, 0) * mm, "mid": v(-41.42, -5.66) * mm, "end": v(-35.76, -8) * mm});
            skPoint(sketch, "E322.visualSharp", {"position": v(-43.76, 8) * mm});
            skArc(sketch, "E322.filletArc", {"start": v(-35.76, 8) * mm, "mid": v(-41.42, 5.66) * mm, "end": v(-43.76, 0) * mm});
            skPoint(sketch, "E323", {"position": v(49.24, 0) * mm});
            skPoint(sketch, "E324.visualSharp", {"position": v(49.24, 8) * mm});
            skArc(sketch, "E324.filletArc", {"start": v(49.24, 0) * mm, "mid": v(46.9, 5.66) * mm, "end": v(41.24, 8) * mm});
            skPoint(sketch, "E325.visualSharp", {"position": v(49.24, -8) * mm});
            skArc(sketch, "E325.filletArc", {"start": v(41.24, -8) * mm, "mid": v(46.9, -5.66) * mm, "end": v(49.24, 0) * mm});
            skCircle(sketch, "E326", {"center": v(45.05, 0) * mm, "radius": 2 * mm});
            skSolve(sketch);
        }
        {
            var Q0;
            Q0=makeQuery(id+"F1.imprint","IMPRINT",FACE,{"disambiguationData":[TD([[makeQuery(id+"F1.imprint","IMPRINT",EDGE,{"derivedFrom":sQuery(id+"F1.wireOp",EDGE,"E320.bottom")}),-1.0]])]});
            extrude(context, id + "F2", {"entities" : qUnion([Q0]), "depth" : 5 * mm});
        }
        {
            var Q0;
            Q0 = qSketchRegion(id + "F0", true);
            extrude(context, id + "F3", {"entities" : qUnion([Q0]), "operationType" : NewBodyOperationType.REMOVE, "depth" : 28.8 * mm, "hasSecondDirection" : true, "secondDirectionOppositeDirection" : false, "secondDirectionDepth" : 3.8 * mm});
        }
        {
            var Q0;
            Q0=makeQuery(id+"F2.opExtrude","CAP_EDGE",EDGE,{"disambiguationData":[OSD([sQuery(id+"F1.wireOp",EDGE,"E326")])],"isStart":false});
            var Q1;
            Q1=makeQuery(id+"F2.opExtrude","CAP_EDGE",EDGE,{"disambiguationData":[OSD([sQuery(id+"F1.wireOp",EDGE,"E326")])],"isStart":true});
            chamfer(context, id + "F4", {"entities" : qUnion([Q0, Q1]), "width" : 1 * mm, "tangentPropagation" : true});
        }
    });
